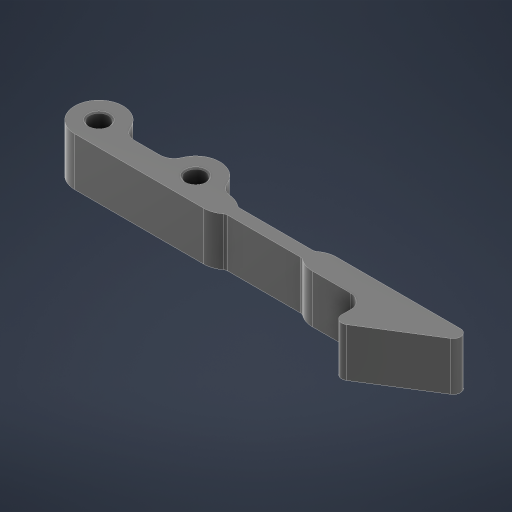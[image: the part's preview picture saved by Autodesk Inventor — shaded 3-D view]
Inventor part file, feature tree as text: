
AUTODESK INVENTOR PART (.ipt)
format: ipt  version: 2024 (Build 280153000, 153)  size: 265,728 bytes
history: native  units: mm
features: sketch x3, extrude x2, chamfer x1, fillet x1, projected_geometry x1
ambient origin geometry x8: Origin, YZ Plane, XZ Plane, XY Plane, X Axis, Y Axis, Z Axis, Center Point
bodies: Solid1 (feature_tree)
feature tree (8):
  extrude  "Extrusion1"  Depth=4.0mm
  chamfer  "Chamfer1"  Distance=3.0mm
  sketch  "Sketch2"  dims[d5=10.0mm]
  extrude  "Extrusion2"  Depth=5.0mm
  fillet  "Fillet2"  Radius=12.5mm
  sketch  "Sketch1"  dims[d0=4.0mm d4=4.0mm]
  projected_geometry  "Projected Loop1"
  sketch  "Sketch3"  dims[d6=10.0mm d7=3.0mm d8=80.0mm d9=12.5mm d10=20.0mm d11=60.0mm d12=3.0mm d13=1.5mm d14=10.0mm d15=0.0mm d16=0.25mm d17=2.0mm d18=45.0deg d19=5.0mm d20=3.0mm d21=3.0mm d22=5.0mm d25=0.0mm d26=0.0mm d28=15.0mm d29=2.5mm d30=15.0mm d31=2.5mm d32=5.0mm]
